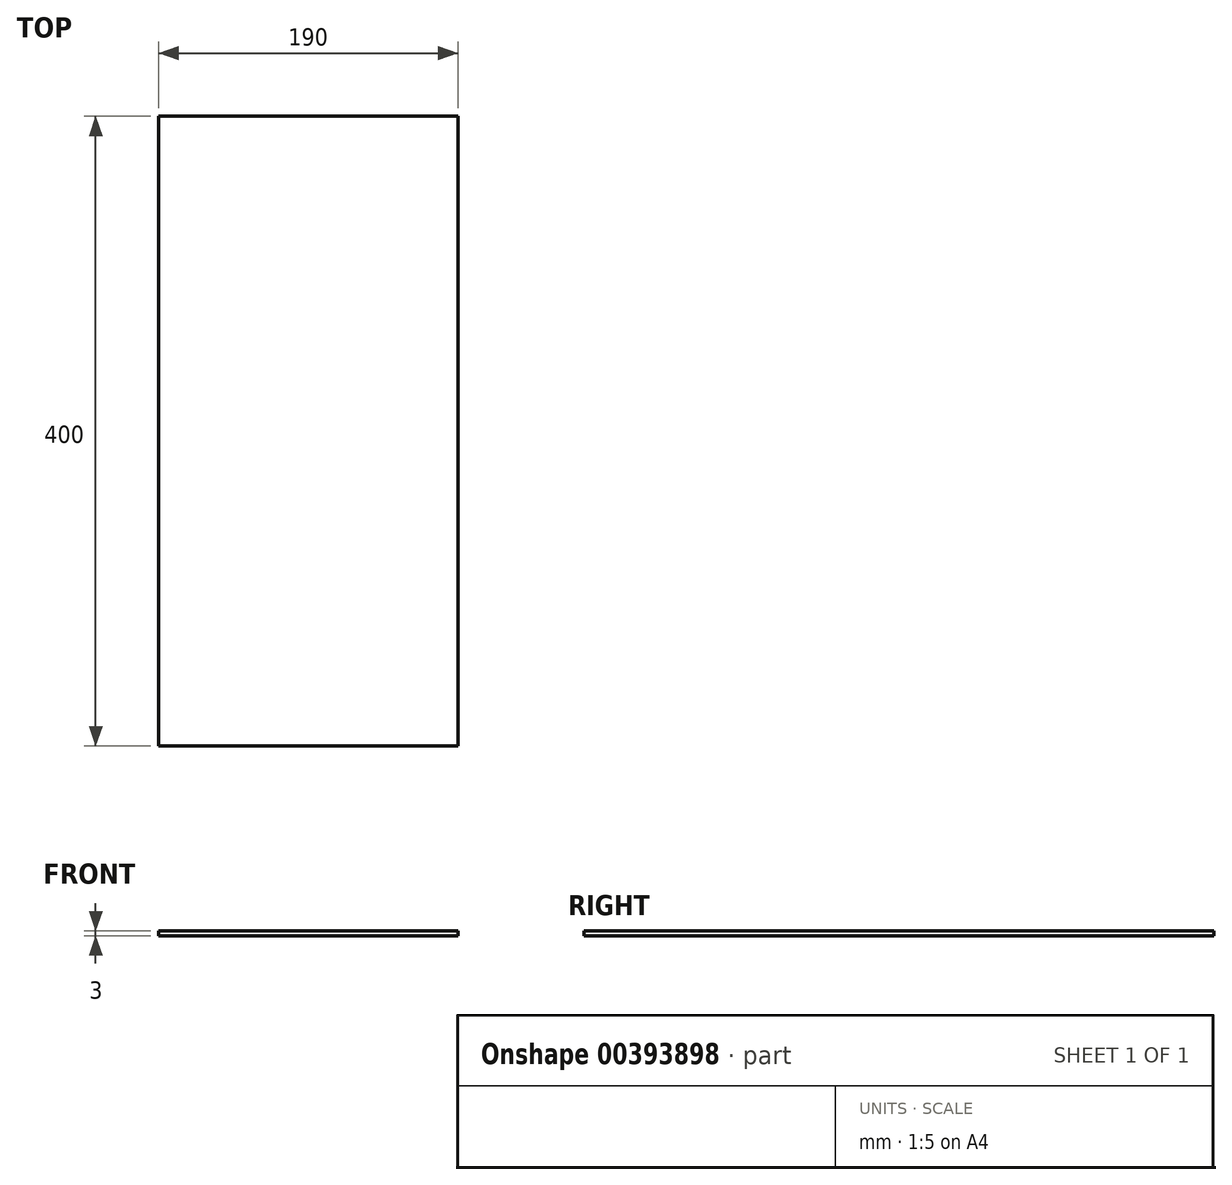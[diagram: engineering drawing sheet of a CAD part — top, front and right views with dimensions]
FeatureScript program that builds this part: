
annotation { "Feature Type Name" : "Feature", "Feature Type Description" : "" }
export const myFeature = defineFeature(function(context is Context, id is Id, definition is map)
    precondition{}
    {
        {
            var Q0;
            Q0=qCreatedBy(makeId("Top.planeOp"),FACE);
            var sketch = newSketch(context, id + "F0", { "sketchPlane" : qUnion([Q0])});
            skLineSegment(sketch, "E0.bottom", {"start": v(95, 200) * mm, "end": v(-95, 200) * mm});
            skLineSegment(sketch, "E0.top", {"start": v(95, -200) * mm, "end": v(-95, -200) * mm});
            skLineSegment(sketch, "E0.left", {"start": v(95, 200) * mm, "end": v(95, -200) * mm});
            skLineSegment(sketch, "E0.right", {"start": v(-95, 200) * mm, "end": v(-95, -200) * mm});
            skPoint(sketch, "E0.middle", {"position": v(0, 0) * mm});
            skSolve(sketch);
        }
        {
            var Q0;
            Q0=makeQuery(id+"F0.imprint","IMPRINT",FACE,{"disambiguationData":[TD([[makeQuery(id+"F0.imprint","IMPRINT",EDGE,{"derivedFrom":sQuery(id+"F0.wireOp",EDGE,"E0.bottom")}),1.0]])]});
            extrude(context, id + "F1", {"entities" : qUnion([Q0]), "depth" : 3 * mm});
        }
    });
